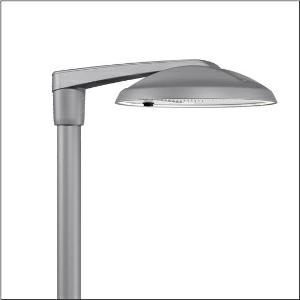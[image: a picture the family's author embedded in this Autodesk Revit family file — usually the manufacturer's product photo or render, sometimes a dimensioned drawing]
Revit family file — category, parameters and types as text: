
# Revit family: dl_r__50_iq_mini___st1_0a_5xa248d31u08ne_2837
name_source: partatom
category: Lighting Fixtures
units: mm (PartAtom-declared; Revit-internal decimal feet)

## family parameters
Cut with Voids When Loaded = No
Host = Face
Light Source = No
Part Type = Normal
Room Calculation Point = No
Round Connector Dimension = Use Diameter
Shared = No

## types (1)
- --- (1 x LED, 17900 lm, 110.1 W, 3000K)
    Apparent Load = 110 VA
    CIE Flux Codes = 37 72 97 100 100
    Color Rendering = 70
    Color Temperature = 3000K
    Default Elevation = 1800 mm
    Description = DL® 50 iQ mini, mast luminaire, primary light control with lens, of PMMA, primary optical cover: cover, of toughened safety glass, transparent, light distribution: ST1.0a, light emission: direct distribution, primary light characteristic: asymmetric, installation type: post-top, side-entry, LED, High Power LED, rated luminous flux: 17.900lm, luminous efficacy: 163lm/W, light colour: 730, colour temperature: 3000K, control: optimised constant luminous flux control (CLO 2.0), Desk-Remote (wireless, voltage-free reading and setting of iQ features in the workshop via application-optimized NFC function/RFID function), Light-Fading, Smart-Wire, Night-Set, Lumen-Switch, Temp-Guard, Auto-Match, Street-Remote, pre-setting: logarithmic dimming characteristic, mains connection: 220..240V, AC, 50/60Hz, connection cable pre-assembled, cable length: 10,5m, start of lifetime: 110W, end of service life: 116W, reduction: 50W, luminaire housing, of diecast aluminium, powder-coated, Siteco® metallic grey (DB 702S), inclination adjustable: 0°, 5°, 10° (post-top) | 0°, -5°, -10°, -15° (side-entry), please order mast post-top element or mast side-entry element separately, diameter: 500mm, height: 115mm, post-top: for spigot size d x l = 76 x 100mm; with reducer (optional accessory) 60 x 100mm | side-entry: for spigot size d x l = 60 x 100mm; with reducer (optional accessory) 42 x 100mm, Smart Interface below, protection rating (complete): IP66, insulation class (complete): insulation class II (safety insulation), certification: CE, ENEC, ENEC+, VDE, impact resistance: IK08, permissible operating ambient temperature for outdoor applications: -25..+40°C, standard-compliant lighting for roads and squares, packaging unit: 1 piece

Light Distribution: ST1.0a
    Height = 115 mm
    Lamp = 1 x LED
    Lamp Light Flux = 17900 lm
    Lamp Power = 110.1 W
    Lamp count = 1
    Length = 500 mm
    Luminous efficacy = 163 lm/W
    Manufacturer = Siteco
    ModVariant = No
    Model = 5XA248D31U08NE
    Number of Poles = 1
    OnlyDefault = Yes
    Power Factor = 1
    Product Name = DL® 50 iQ mini | ST1.0a
    Product group = mast luminaire | pylon top
    ProductGroupID = 6100
    Protection Class = Protection class II
    Protection Degree = IP 66
    RLX_Detail_Level = 1
    RLX_Emergency_Light_Flux = 0 lm
    RLX_Emergency_Type = 0
    RLX_Emergency_Type_DB = No
    RlxData = <blob elided: 106513 chars, md5=7c0623eb>
    Socket = socket
    Standby Power = 0 W
    System Light Flux = 17900 lm
    System Power = 110 W
    Type Comments = factory setting: luminous flux: 100 % | dim-lin: 254 | 601 mA
    Type Image = l_1296955.jpg
    URL = http://relux.com
    VarID = @adj_033395
    Voltage = 0 V
    Weight = 0.00 kg
    Width = 0 mm  [stored 0 ft]

note: [stored X ft] marks values corroborated as IEEE doubles in the binary element streams (Revit-internal decimal feet)

## geometry (parser evidence)
native form markers: Blend x4, Sweep x9
no freeform markers — native parametric forms only
